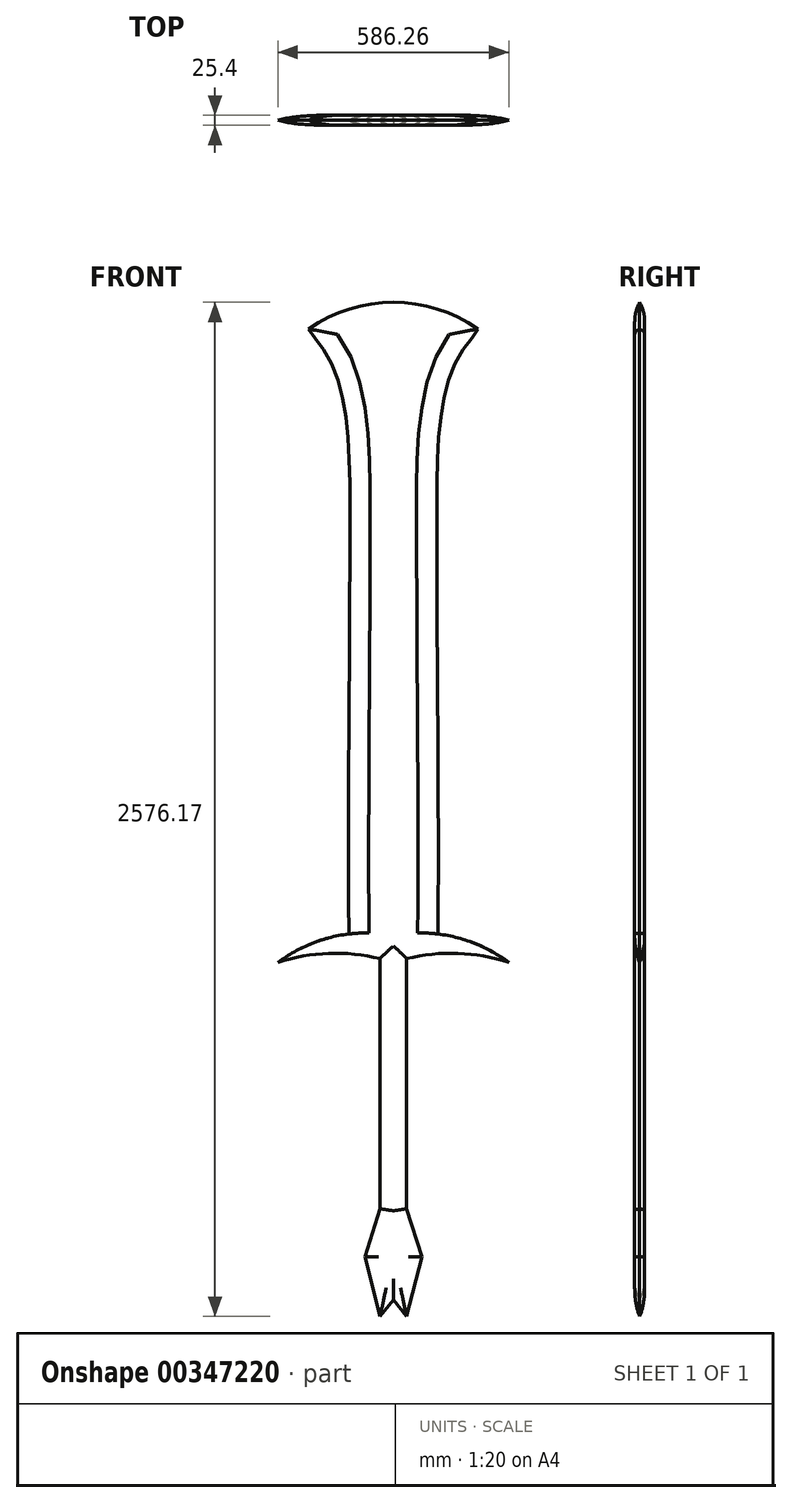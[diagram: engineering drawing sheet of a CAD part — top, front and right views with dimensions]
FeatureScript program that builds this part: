
annotation { "Feature Type Name" : "Feature", "Feature Type Description" : "" }
export const myFeature = defineFeature(function(context is Context, id is Id, definition is map)
    precondition{}
    {
        {
            var Q0;
            Q0=qCreatedBy(makeId("Front.planeOp"),FACE);
            var sketch = newSketch(context, id + "F0", { "sketchPlane" : qUnion([Q0])});
            skLineSegment(sketch, "E0", {"start": v(0, -799.15) * mm, "end": v(0, 724.85) * mm});
            skFitSpline(sketch, "E1", {"points": [v(-112.77, -803.1) * mm, v(-112.77, -257.33) * mm, v(-110.28, 251.05) * mm, v(-120.25, 515.21) * mm, v(-165.1, 669.72) * mm, v(-214.95, 742) * mm], "startDerivative": vector(-26.31, 1896.5) * mm, "endDerivative": vector(-239.26, 448.76) * mm});
            skFitSpline(sketch, "E2.MirrorCS", {"points": [v(112.77, -803.1) * mm, v(112.77, -257.33) * mm, v(110.28, 251.05) * mm, v(120.25, 515.21) * mm, v(165.1, 669.72) * mm, v(214.95, 742) * mm], "startDerivative": vector(26.31, 1896.5) * mm, "endDerivative": vector(239.26, 448.76) * mm});
            skArc(sketch, "E3", {"start": v(214.95, 742) * mm, "mid": v(0, 809.46) * mm, "end": v(-214.95, 742) * mm});
            skArc(sketch, "E4", {"start": v(0, -799.15) * mm, "mid": v(-153.8, -802.58) * mm, "end": v(-293.13, -867.76) * mm});
            skArc(sketch, "E5", {"start": v(0, -867.76) * mm, "mid": v(-146.57, -844.3) * mm, "end": v(-293.13, -867.76) * mm});
            skArc(sketch, "E6.MirrorCS", {"start": v(0, -799.15) * mm, "mid": v(153.8, -802.58) * mm, "end": v(293.13, -867.76) * mm});
            skArc(sketch, "E7.MirrorCS", {"start": v(0, -867.76) * mm, "mid": v(146.57, -844.3) * mm, "end": v(293.13, -867.76) * mm});
            skLineSegment(sketch, "E8", {"start": v(0, -867.76) * mm, "end": v(0, -1493.49) * mm});
            skLineSegment(sketch, "E9", {"start": v(-33.68, -858.07) * mm, "end": v(-33.68, -1493.5) * mm});
            skLineSegment(sketch, "E10.MirrorCS", {"start": v(33.68, -858.07) * mm, "end": v(33.68, -1493.5) * mm});
            skLineSegment(sketch, "E11", {"start": v(-33.68, -1493.5) * mm, "end": v(-72.56, -1615.16) * mm});
            skLineSegment(sketch, "E12", {"start": v(-72.56, -1615.16) * mm, "end": v(-33.68, -1766.7) * mm});
            skLineSegment(sketch, "E13", {"start": v(-33.68, -1766.7) * mm, "end": v(0, -1724.42) * mm});
            skLineSegment(sketch, "E14.MirrorCS", {"start": v(33.68, -1493.5) * mm, "end": v(72.56, -1615.16) * mm});
            skLineSegment(sketch, "E15.MirrorCS", {"start": v(72.56, -1615.16) * mm, "end": v(33.68, -1766.7) * mm});
            skLineSegment(sketch, "E16.MirrorCS", {"start": v(33.68, -1766.7) * mm, "end": v(0, -1724.42) * mm});
            skSolve(sketch);
        }
        {
            var Q0;
            {var subQ5=sQuery(id+"F0.wireOp",EDGE,"E3");Q0=makeQuery(id+"F0.imprint","IMPRINT",FACE,{"disambiguationData":[TD([[makeQuery(id+"F0.imprint","IMPRINT",EDGE,{"derivedFrom":subQ5}),1.0]])]});}
            var Q1;
            {var subQ1=sQuery(id+"F0.wireOp",EDGE,"E4");var subQ7=sQuery(id+"F0.wireOp",EDGE,"E6.MirrorCS");var subQ8=makeQuery(id+"F0.imprint","INTERSECT",VERTEX,{"derivedFrom":[subQ1,subQ7]});Q1=makeQuery(id+"F0.imprint","IMPRINT",FACE,{"disambiguationData":[TD([[makeQuery(id+"F0.imprint","IMPRINT",EDGE,{"disambiguationData":[TD([[subQ8,-1.0]])],"derivedFrom":subQ1}),1.0]])]});}
            var Q2;
            {var subQ1=sQuery(id+"F0.wireOp",EDGE,"E9");Q2=makeQuery(id+"F0.imprint","IMPRINT",FACE,{"disambiguationData":[TD([[makeQuery(id+"F0.imprint","IMPRINT",EDGE,{"derivedFrom":subQ1}),1.0]])]});}
            extrude(context, id + "F1", {"entities" : qUnion([Q0, Q1, Q2]), "depth" : 12.7 * mm});
        }
        {
            var Q0;
            Q0=makeQuery(id+"F1.opExtrude","CAP_EDGE",EDGE,{"disambiguationData":[OSD([sQuery(id+"F0.wireOp",EDGE,"E1")])],"isStart":false});
            var Q1;
            Q1=makeQuery(id+"F1.opExtrude","CAP_EDGE",EDGE,{"disambiguationData":[OSD([sQuery(id+"F0.wireOp",EDGE,"E2.MirrorCS")])],"isStart":false});
            fillet(context, id + "F2", {"entities" : qUnion([Q0, Q1]), "radius" : 110.38 * mm, "tangentPropagation" : true, "allowEdgeOverflow" : false});
        }
        {
            var Q0;
            Q0=makeQuery(id+"F1.opExtrude","CAP_EDGE",EDGE,{"disambiguationData":[OSD([sQuery(id+"F0.wireOp",EDGE,"E3")])],"isStart":false});
            fillet(context, id + "F3", {"entities" : qUnion([Q0]), "radius" : 104.25 * mm, "tangentPropagation" : true, "allowEdgeOverflow" : false});
        }
        {
            var Q0;
            Q0=makeQuery(id+"F1.opExtrude","CAP_EDGE",EDGE,{"disambiguationData":[OSD([sQuery(id+"F0.wireOp",EDGE,"E7.MirrorCS")])],"isStart":false});
            var Q1;
            Q1=makeQuery(id+"F1.opExtrude","CAP_EDGE",EDGE,{"disambiguationData":[OSD([sQuery(id+"F0.wireOp",EDGE,"E5")])],"isStart":false});
            fillet(context, id + "F4", {"entities" : qUnion([Q0, Q1]), "radius" : 67.45 * mm, "tangentPropagation" : true, "allowEdgeOverflow" : false});
        }
        {
            var Q0;
            Q0=makeQuery(id+"F1.opExtrude","CAP_EDGE",EDGE,{"disambiguationData":[OSD([sQuery(id+"F0.wireOp",EDGE,"E10.MirrorCS")])],"isStart":false});
            var Q1;
            Q1=makeQuery(id+"F1.opExtrude","CAP_EDGE",EDGE,{"disambiguationData":[OSD([sQuery(id+"F0.wireOp",EDGE,"E9")])],"isStart":false});
            var Q2;
            Q2=makeQuery(id+"F1.opExtrude","CAP_EDGE",EDGE,{"disambiguationData":[OSD([sQuery(id+"F0.wireOp",EDGE,"E11")])],"isStart":false});
            var Q3;
            Q3=makeQuery(id+"F1.opExtrude","CAP_EDGE",EDGE,{"disambiguationData":[OSD([sQuery(id+"F0.wireOp",EDGE,"E12")])],"isStart":false});
            var Q4;
            Q4=makeQuery(id+"F1.opExtrude","CAP_EDGE",EDGE,{"disambiguationData":[OSD([sQuery(id+"F0.wireOp",EDGE,"E13")])],"isStart":false});
            var Q5;
            Q5=makeQuery(id+"F1.opExtrude","CAP_EDGE",EDGE,{"disambiguationData":[OSD([sQuery(id+"F0.wireOp",EDGE,"E16.MirrorCS")])],"isStart":false});
            var Q6;
            Q6=makeQuery(id+"F1.opExtrude","CAP_EDGE",EDGE,{"disambiguationData":[OSD([sQuery(id+"F0.wireOp",EDGE,"E15.MirrorCS")])],"isStart":false});
            var Q7;
            Q7=makeQuery(id+"F1.opExtrude","CAP_EDGE",EDGE,{"disambiguationData":[OSD([sQuery(id+"F0.wireOp",EDGE,"E14.MirrorCS")])],"isStart":false});
            fillet(context, id + "F5", {"entities" : qUnion([Q0, Q1, Q2, Q3, Q4, Q5, Q6, Q7]), "radius" : 49.06 * mm, "tangentPropagation" : true, "allowEdgeOverflow" : false});
        }
        {
            var Q0;
            Q0=makeQuery(id+"F1.opExtrude","SWEPT_BODY",BODY,{"disambiguationData":[OSD([sQuery(id+"F0.wireOp",EDGE,"E1"),sQuery(id+"F0.wireOp",EDGE,"E2.MirrorCS"),sQuery(id+"F0.wireOp",EDGE,"E3"),sQuery(id+"F0.wireOp",EDGE,"E4"),sQuery(id+"F0.wireOp",EDGE,"E5"),sQuery(id+"F0.wireOp",EDGE,"E6.MirrorCS"),sQuery(id+"F0.wireOp",EDGE,"E7.MirrorCS"),sQuery(id+"F0.wireOp",EDGE,"E9"),sQuery(id+"F0.wireOp",EDGE,"E10.MirrorCS"),sQuery(id+"F0.wireOp",EDGE,"E11"),sQuery(id+"F0.wireOp",EDGE,"E12"),sQuery(id+"F0.wireOp",EDGE,"E13"),sQuery(id+"F0.wireOp",EDGE,"E14.MirrorCS"),sQuery(id+"F0.wireOp",EDGE,"E15.MirrorCS"),sQuery(id+"F0.wireOp",EDGE,"E16.MirrorCS")])]});
            transform(context, id + "F6", {"entities" : qUnion([Q0]), "transformType" : TransformType.COPY});
        }
        {
            var Q0;
            Q0=makeQuery(id+"F1.opExtrude","CAP_FACE",FACE,{"disambiguationData":[OSD([sQuery(id+"F0.wireOp",EDGE,"E1"),sQuery(id+"F0.wireOp",EDGE,"E2.MirrorCS"),sQuery(id+"F0.wireOp",EDGE,"E3"),sQuery(id+"F0.wireOp",EDGE,"E4"),sQuery(id+"F0.wireOp",EDGE,"E5"),sQuery(id+"F0.wireOp",EDGE,"E6.MirrorCS"),sQuery(id+"F0.wireOp",EDGE,"E7.MirrorCS"),sQuery(id+"F0.wireOp",EDGE,"E9"),sQuery(id+"F0.wireOp",EDGE,"E10.MirrorCS"),sQuery(id+"F0.wireOp",EDGE,"E11"),sQuery(id+"F0.wireOp",EDGE,"E12"),sQuery(id+"F0.wireOp",EDGE,"E13"),sQuery(id+"F0.wireOp",EDGE,"E14.MirrorCS"),sQuery(id+"F0.wireOp",EDGE,"E15.MirrorCS"),sQuery(id+"F0.wireOp",EDGE,"E16.MirrorCS")])],"isStart":true});
            var sketch = newSketch(context, id + "F7", { "sketchPlane" : qUnion([Q0])});
            skLineSegment(sketch, "E17", {"start": v(0, 0) * mm, "end": v(0, 57.18) * mm});
            skSolve(sketch);
        }
        {
            var Q0;
            Q0=makeQuery(id+"F1.opExtrude","SWEPT_BODY",BODY,{"disambiguationData":[OSD([sQuery(id+"F0.wireOp",EDGE,"E1"),sQuery(id+"F0.wireOp",EDGE,"E2.MirrorCS"),sQuery(id+"F0.wireOp",EDGE,"E3"),sQuery(id+"F0.wireOp",EDGE,"E4"),sQuery(id+"F0.wireOp",EDGE,"E5"),sQuery(id+"F0.wireOp",EDGE,"E6.MirrorCS"),sQuery(id+"F0.wireOp",EDGE,"E7.MirrorCS"),sQuery(id+"F0.wireOp",EDGE,"E9"),sQuery(id+"F0.wireOp",EDGE,"E10.MirrorCS"),sQuery(id+"F0.wireOp",EDGE,"E11"),sQuery(id+"F0.wireOp",EDGE,"E12"),sQuery(id+"F0.wireOp",EDGE,"E13"),sQuery(id+"F0.wireOp",EDGE,"E14.MirrorCS"),sQuery(id+"F0.wireOp",EDGE,"E15.MirrorCS"),sQuery(id+"F0.wireOp",EDGE,"E16.MirrorCS")])]});
            var Q1;
            Q1=sQuery(id+"F7.wireOp",EDGE,"E17");
            transform(context, id + "F8", {"entities" : qUnion([Q0]), "transformType" : TransformType.ROTATION, "transformAxis" : qUnion([Q1]), "angle" : 180 * degree, "makeCopy" : false});
        }
    });
